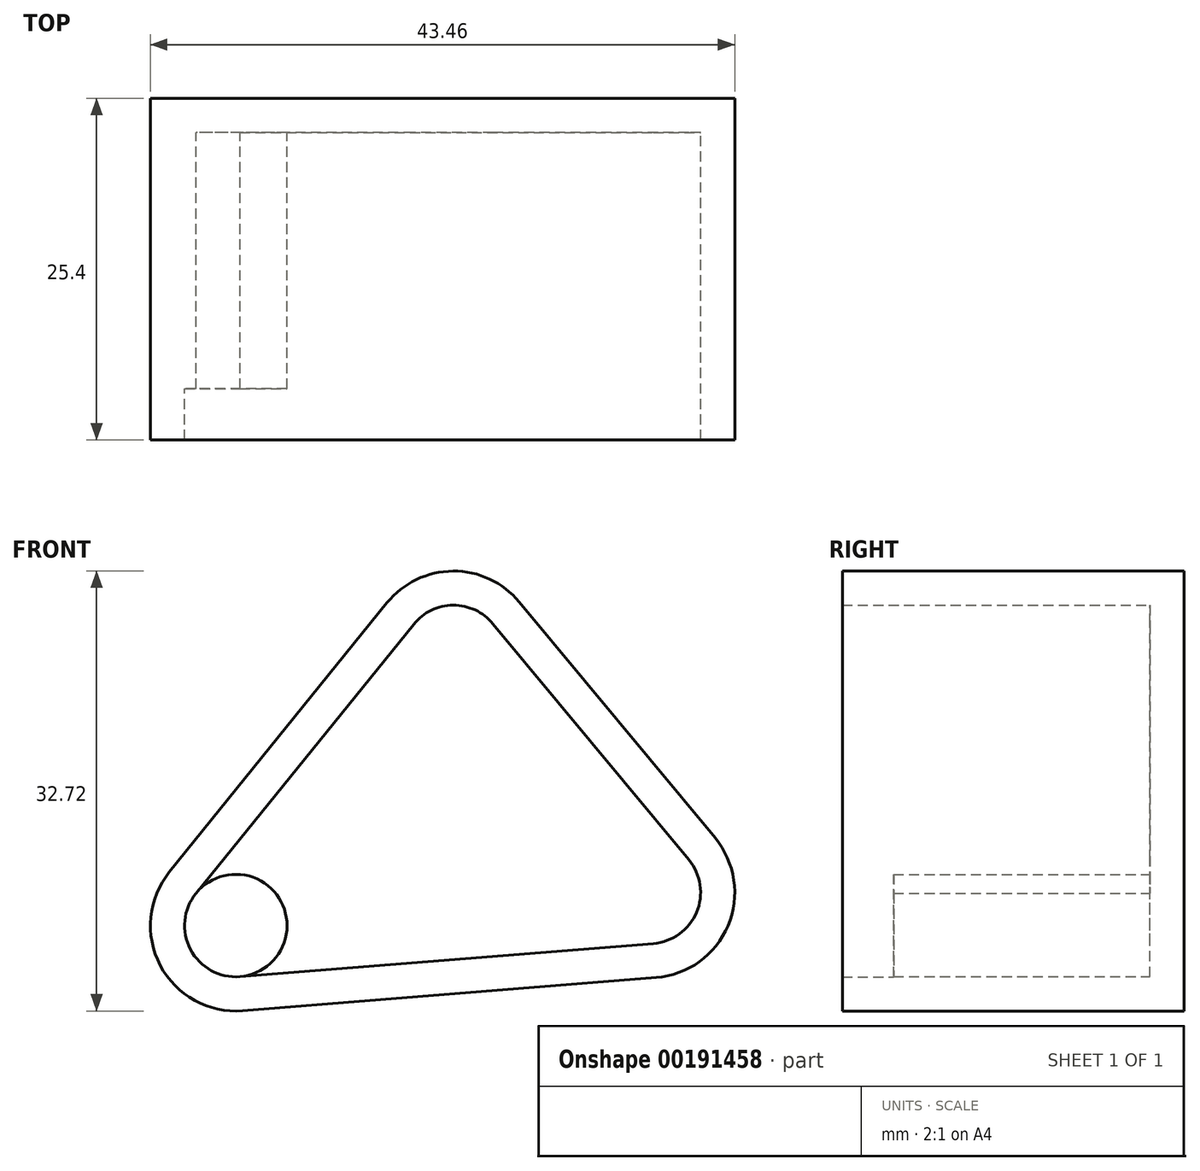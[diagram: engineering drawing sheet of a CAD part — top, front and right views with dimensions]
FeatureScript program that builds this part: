
annotation { "Feature Type Name" : "Feature", "Feature Type Description" : "" }
export const myFeature = defineFeature(function(context is Context, id is Id, definition is map)
    precondition{}
    {
        {
            var Q0;
            Q0=qCreatedBy(makeId("Front.planeOp"),FACE);
            var sketch = newSketch(context, id + "F0", { "sketchPlane" : qUnion([Q0])});
            skLineSegment(sketch, "E0", {"start": v(-7.8, 9.4) * mm, "end": v(-22.37, 26.96) * mm});
            skLineSegment(sketch, "E1", {"start": v(-32.2, 26.9) * mm, "end": v(-48.38, 6.89) * mm});
            skLineSegment(sketch, "E2", {"start": v(-42.94, -3.44) * mm, "end": v(-12.19, -0.98) * mm});
            skPoint(sketch, "E3.visualSharp", {"position": v(-27.32, 32.93) * mm});
            skArc(sketch, "E3.filletArc", {"start": v(-22.37, 26.96) * mm, "mid": v(-27.3, 29.26) * mm, "end": v(-32.2, 26.9) * mm});
            skPoint(sketch, "E4.visualSharp", {"position": v(0, 0) * mm});
            skArc(sketch, "E4.filletArc", {"start": v(-12.19, -0.98) * mm, "mid": v(-6.84, 2.89) * mm, "end": v(-7.8, 9.4) * mm});
            skPoint(sketch, "E5.visualSharp", {"position": v(-57.7, -4.62) * mm});
            skArc(sketch, "E5.filletArc", {"start": v(-48.38, 6.89) * mm, "mid": v(-49.06, -0.07) * mm, "end": v(-42.94, -3.44) * mm});
            skSolve(sketch);
        }
        {
            var Q0;
            Q0 = qSketchRegion(id + "F0", true);
            extrude(context, id + "F1", {"entities" : qUnion([Q0]), "depth" : 25.4 * mm});
        }
        {
            var Q0;
            Q0=makeQuery(id+"F1.opExtrude","CAP_FACE",FACE,{"disambiguationData":[OSD([sQuery(id+"F0.wireOp",EDGE,"E0"),sQuery(id+"F0.wireOp",EDGE,"E1"),sQuery(id+"F0.wireOp",EDGE,"E2"),sQuery(id+"F0.wireOp",EDGE,"E3.filletArc"),sQuery(id+"F0.wireOp",EDGE,"E4.filletArc"),sQuery(id+"F0.wireOp",EDGE,"E5.filletArc")])],"isStart":false});
            shell(context, id + "F2", {"entities" : qUnion([Q0]), "thickness" : 2.54 * mm});
        }
        {
            var Q0;
            Q0=makeQuery(id+"F2.opShell","OFFSET_FACE",FACE,{"disambiguationData":[OSD([sQuery(id+"F0.wireOp",EDGE,"E0"),sQuery(id+"F0.wireOp",EDGE,"E1"),sQuery(id+"F0.wireOp",EDGE,"E2"),sQuery(id+"F0.wireOp",EDGE,"E3.filletArc"),sQuery(id+"F0.wireOp",EDGE,"E4.filletArc"),sQuery(id+"F0.wireOp",EDGE,"E5.filletArc")])]});
            var sketch = newSketch(context, id + "F3", { "sketchPlane" : qUnion([Q0])});
            skCircle(sketch, "E6", {"center": v(-43.45, 2.9) * mm, "radius": 3.81 * mm});
            skSolve(sketch);
        }
        {
            var Q0;
            Q0 = qSketchRegion(id + "F3", true);
            extrude(context, id + "F4", {"entities" : qUnion([Q0]), "operationType" : NewBodyOperationType.ADD, "depth" : 19.05 * mm});
        }
        {
            var Q0;
            Q0=makeQuery(id+"F2.opShell","OFFSET_FACE",FACE,{"disambiguationData":[OSD([sQuery(id+"F0.wireOp",EDGE,"E0"),sQuery(id+"F0.wireOp",EDGE,"E1"),sQuery(id+"F0.wireOp",EDGE,"E2"),sQuery(id+"F0.wireOp",EDGE,"E3.filletArc"),sQuery(id+"F0.wireOp",EDGE,"E4.filletArc"),sQuery(id+"F0.wireOp",EDGE,"E5.filletArc")])]});
            var sketch = newSketch(context, id + "F5", { "sketchPlane" : qUnion([Q0])});
            skCircle(sketch, "E7", {"center": v(-27.25, 22.9) * mm, "radius": 3.58 * mm});
            skCircle(sketch, "E8", {"center": v(-12.7, 5.35) * mm, "radius": 3.38 * mm});
            skSolve(sketch);
        }
        {
            var Q0;
            Q0=sQuery(id+"F5.wireOp",EDGE,"E7");
            var Q1;
            Q1=sQuery(id+"F5.wireOp",EDGE,"E8");
            extrude(context, id + "F6", {"bodyType" : ToolBodyType.SURFACE, "surfaceEntities" : qUnion([Q0, Q1]), "depth" : 19.05 * mm});
        }
    });
